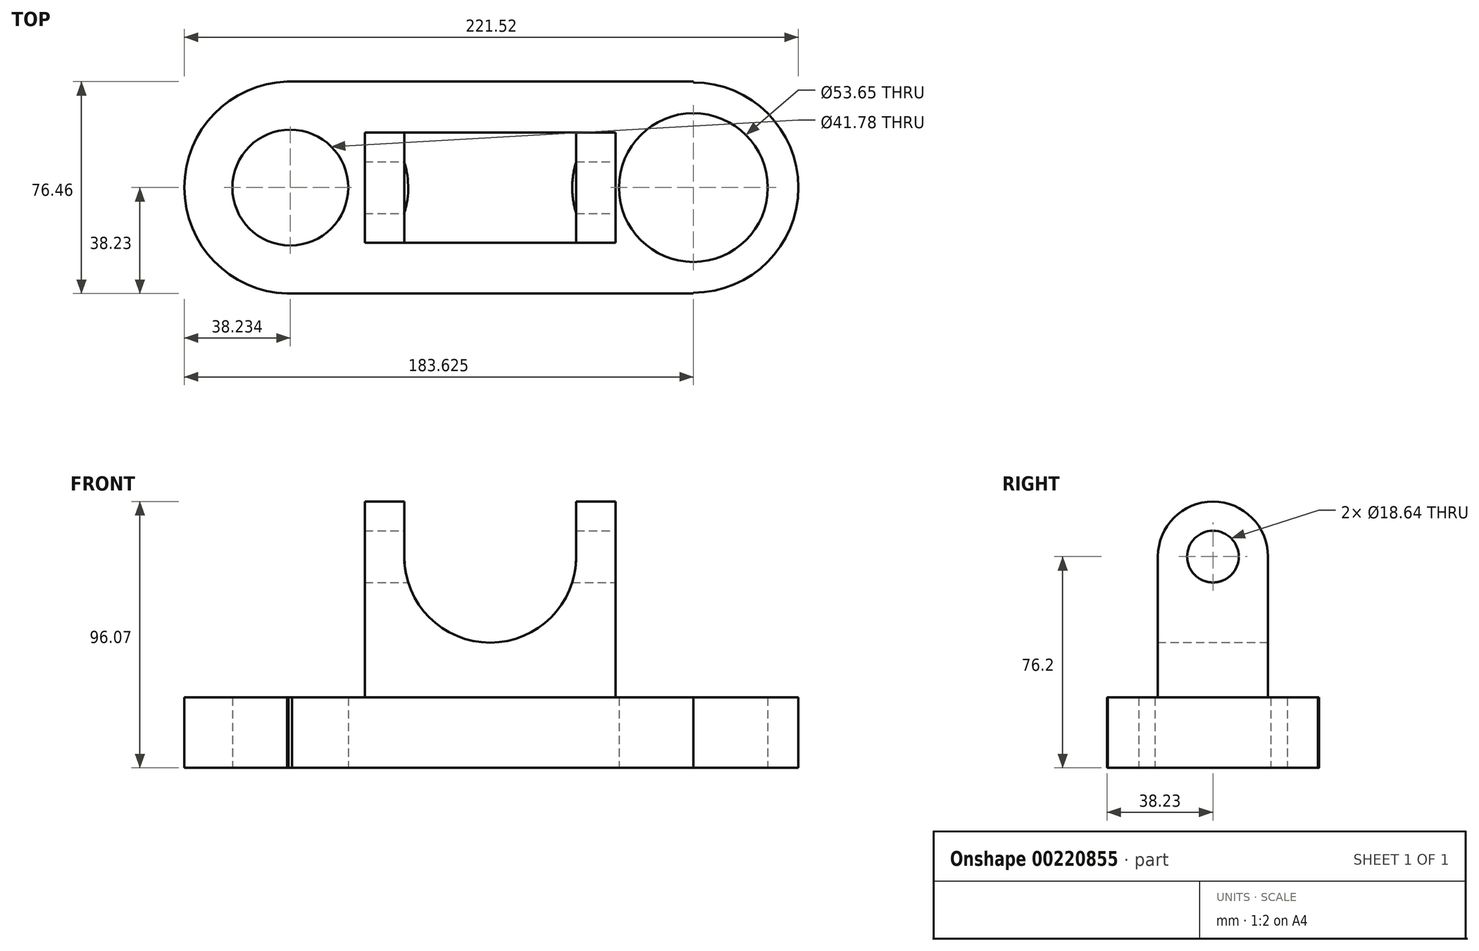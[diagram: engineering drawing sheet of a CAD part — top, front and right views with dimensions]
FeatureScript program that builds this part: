
annotation { "Feature Type Name" : "Feature", "Feature Type Description" : "" }
export const myFeature = defineFeature(function(context is Context, id is Id, definition is map)
    precondition{}
    {
        {
            var Q0;
            Q0=qCreatedBy(makeId("Top.planeOp"),FACE);
            var sketch = newSketch(context, id + "F0", { "sketchPlane" : qUnion([Q0])});
            skCircle(sketch, "E0", {"center": v(-72.1, 0) * mm, "radius": 38.23 * mm});
            skLineSegment(sketch, "E1.bottom", {"start": v(73.29, -38.23) * mm, "end": v(-73.29, -38.23) * mm});
            skLineSegment(sketch, "E1.top", {"start": v(73.29, 38.23) * mm, "end": v(-73.29, 38.23) * mm});
            skLineSegment(sketch, "E1.left", {"start": v(73.29, -38.23) * mm, "end": v(73.29, 38.23) * mm});
            skLineSegment(sketch, "E1.right", {"start": v(-73.29, -38.23) * mm, "end": v(-73.29, 38.23) * mm});
            skPoint(sketch, "E1.middle", {"position": v(0, 0) * mm});
            skCircle(sketch, "E2", {"center": v(73.29, 0) * mm, "radius": 37.9 * mm});
            skCircle(sketch, "E3", {"center": v(-72.1, 0) * mm, "radius": 20.9 * mm});
            skCircle(sketch, "E4", {"center": v(73.29, 0) * mm, "radius": 26.83 * mm});
            skLineSegment(sketch, "E5.bottom", {"start": v(45.22, -19.87) * mm, "end": v(-45.22, -19.87) * mm});
            skLineSegment(sketch, "E5.top", {"start": v(45.22, 19.87) * mm, "end": v(-45.22, 19.87) * mm});
            skLineSegment(sketch, "E5.left", {"start": v(45.22, -19.87) * mm, "end": v(45.22, 19.87) * mm});
            skLineSegment(sketch, "E5.right", {"start": v(-45.22, -19.87) * mm, "end": v(-45.22, 19.87) * mm});
            skSolve(sketch);
        }
        {
            var Q0;
            {var subQ0=sQuery(id+"F0.wireOp",EDGE,"E5.top");var subQ1=sQuery(id+"F0.wireOp",EDGE,"E0");var subQ2=makeQuery(id+"F0.imprint","INTERSECT",VERTEX,{"derivedFrom":[subQ1,subQ0]});Q0=makeQuery(id+"F0.imprint","IMPRINT",FACE,{"disambiguationData":[TD([[makeQuery(id+"F0.imprint","IMPRINT",EDGE,{"disambiguationData":[TD([[subQ2,1.0]])],"derivedFrom":subQ1}),-1.0]])]});}
            var Q1;
            {var subQ5=sQuery(id+"F0.wireOp",EDGE,"E5.right");Q1=makeQuery(id+"F0.imprint","IMPRINT",FACE,{"disambiguationData":[TD([[makeQuery(id+"F0.imprint","IMPRINT",EDGE,{"derivedFrom":subQ5}),-1.0]])]});}
            var Q2;
            {var subQ5=sQuery(id+"F0.wireOp",EDGE,"E5.left");Q2=makeQuery(id+"F0.imprint","IMPRINT",FACE,{"disambiguationData":[TD([[makeQuery(id+"F0.imprint","IMPRINT",EDGE,{"derivedFrom":subQ5}),1.0]])]});}
            extrude(context, id + "F1", {"entities" : qUnion([Q0, Q1, Q2]), "depth" : 76.2 * mm});
        }
        {
            var Q0;
            Q0 = qSketchRegion(id + "F0", true);
            extrude(context, id + "F2", {"entities" : qUnion([Q0]), "operationType" : NewBodyOperationType.ADD, "depth" : 25.4 * mm});
        }
        {
            var Q0;
            Q0=makeQuery(id+"F1.opExtrude","SWEPT_FACE",FACE,{"disambiguationData":[OSD([sQuery(id+"F0.wireOp",EDGE,"E5.bottom")])]});
            var sketch = newSketch(context, id + "F3", { "sketchPlane" : qUnion([Q0])});
            skCircle(sketch, "E6", {"center": v(0, 76.2) * mm, "radius": 31.01 * mm});
            skSolve(sketch);
        }
        {
            var Q0;
            Q0 = qSketchRegion(id + "F3", true);
            extrude(context, id + "F4", {"entities" : qUnion([Q0]), "operationType" : NewBodyOperationType.REMOVE, "oppositeDirection" : true, "depth" : 48.77 * mm});
        }
        {
            var Q0;
            {var subQ0=sQuery(id+"F0.wireOp",EDGE,"E5.bottom");var subQ1=sQuery(id+"F0.wireOp",EDGE,"E5.top");var subQ2=sQuery(id+"F0.wireOp",EDGE,"E5.right");Q0=makeQuery(id+"F4.boolean.opBoolean","SPLIT",FACE,{"disambiguationData":[TD([makeQuery(id+"F1.opExtrude","SWEPT_FACE",FACE,{"disambiguationData":[OSD([subQ2])]})])],"derivedFrom":makeQuery(id+"F1.opExtrude","CAP_FACE",FACE,{"disambiguationData":[OSD([subQ0,subQ1,sQuery(id+"F0.wireOp",EDGE,"E5.left"),subQ2])],"isStart":false})});}
            var sketch = newSketch(context, id + "F5", { "sketchPlane" : qUnion([Q0])});
            skLineSegment(sketch, "E7.bottom", {"start": v(-45.22, 19.87) * mm, "end": v(-31.01, 19.87) * mm});
            skLineSegment(sketch, "E7.top", {"start": v(-45.22, 0) * mm, "end": v(-31.01, 0) * mm});
            skLineSegment(sketch, "E7.left", {"start": v(-45.22, 19.87) * mm, "end": v(-45.22, 0) * mm});
            skLineSegment(sketch, "E7.right", {"start": v(-31.01, 19.87) * mm, "end": v(-31.01, 0) * mm});
            skSolve(sketch);
        }
        {
            var Q0;
            Q0=makeQuery(id+"F5.imprint","IMPRINT",FACE,{"disambiguationData":[TD([[makeQuery(id+"F5.imprint","IMPRINT",EDGE,{"derivedFrom":sQuery(id+"F5.wireOp",EDGE,"E7.bottom")}),1.0]])]});
            var Q1;
            Q1=sQuery(id+"F5.wireOp",EDGE,"E7.top");
            revolve(context, id + "F6", {"operationType" : NewBodyOperationType.ADD, "entities" : qUnion([Q0]), "axis" : qUnion([Q1]), "revolveType" : RevolveType.FULL});
        }
        {
            var Q0;
            {var subQ0=sQuery(id+"F0.wireOp",EDGE,"E5.bottom");var subQ1=sQuery(id+"F0.wireOp",EDGE,"E5.top");var subQ2=sQuery(id+"F0.wireOp",EDGE,"E5.left");Q0=makeQuery(id+"F4.boolean.opBoolean","SPLIT",FACE,{"disambiguationData":[TD([makeQuery(id+"F1.opExtrude","SWEPT_FACE",FACE,{"disambiguationData":[OSD([subQ2])]})])],"derivedFrom":makeQuery(id+"F1.opExtrude","CAP_FACE",FACE,{"disambiguationData":[OSD([subQ0,subQ1,subQ2,sQuery(id+"F0.wireOp",EDGE,"E5.right")])],"isStart":false})});}
            var sketch = newSketch(context, id + "F7", { "sketchPlane" : qUnion([Q0])});
            skLineSegment(sketch, "E8.bottom", {"start": v(31.01, 19.87) * mm, "end": v(45.22, 19.87) * mm});
            skLineSegment(sketch, "E8.top", {"start": v(31.01, 0) * mm, "end": v(45.22, 0) * mm});
            skLineSegment(sketch, "E8.left", {"start": v(31.01, 19.87) * mm, "end": v(31.01, 0) * mm});
            skLineSegment(sketch, "E8.right", {"start": v(45.22, 19.87) * mm, "end": v(45.22, 0) * mm});
            skSolve(sketch);
        }
        {
            var Q0;
            Q0=makeQuery(id+"F7.imprint","IMPRINT",FACE,{"disambiguationData":[TD([[makeQuery(id+"F7.imprint","IMPRINT",EDGE,{"derivedFrom":sQuery(id+"F7.wireOp",EDGE,"E8.bottom")}),1.0]])]});
            var Q1;
            Q1=sQuery(id+"F7.wireOp",EDGE,"E8.top");
            revolve(context, id + "F8", {"operationType" : NewBodyOperationType.ADD, "entities" : qUnion([Q0]), "axis" : qUnion([Q1]), "revolveType" : RevolveType.FULL});
        }
        {
            var Q0;
            Q0=makeQuery(id+"F8.boolean.opBoolean","MERGE",FACE,{"derivedFrom":[makeQuery(id+"F1.opExtrude","SWEPT_FACE",FACE,{"disambiguationData":[OSD([sQuery(id+"F0.wireOp",EDGE,"E5.left")])]}),makeQuery(id+"F8.opRevolve","SWEPT_FACE",FACE,{"disambiguationData":[OSD([sQuery(id+"F7.wireOp",EDGE,"E8.right")])]})]});
            var sketch = newSketch(context, id + "F9", { "sketchPlane" : qUnion([Q0])});
            skCircle(sketch, "E9", {"center": v(0, 76.2) * mm, "radius": 9.32 * mm});
            skSolve(sketch);
        }
        {
            var Q0;
            Q0=makeQuery(id+"F9.imprint","IMPRINT",FACE,{"disambiguationData":[TD([[makeQuery(id+"F9.imprint","IMPRINT",EDGE,{"derivedFrom":sQuery(id+"F9.wireOp",EDGE,"E9")}),1.0]])]});
            extrude(context, id + "F10", {"entities" : qUnion([Q0]), "operationType" : NewBodyOperationType.REMOVE, "oppositeDirection" : true, "depth" : 120.9 * mm});
        }
    });
